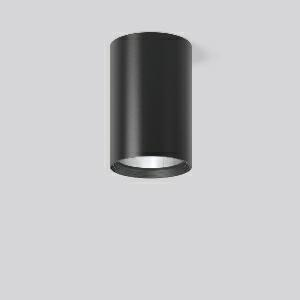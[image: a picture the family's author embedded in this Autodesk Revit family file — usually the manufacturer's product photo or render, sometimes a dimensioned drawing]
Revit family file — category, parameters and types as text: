
# Revit family: heledon_maxi_a_931219_003_3_76_b0ef
name_source: partatom
category: Lighting Fixtures
units: mm (PartAtom-declared; Revit-internal decimal feet)

## family parameters
Cut with Voids When Loaded = No
Host = Face
Light Source = No
Part Type = Normal
Room Calculation Point = No
Round Connector Dimension = Use Diameter
Shared = No

## types (1)
- HELEDON maxi A (1 x LED Modul 935, 3250 lm, 3500)
    Apparent Load = 25 VA
    Approval mark = CE
    CIE Flux Codes = 97 100 100 100 100
    Color Rendering = 92
    Color Temperature = 3500
    Default Elevation = 1800 mm
    Description = Series: HELEDON maxi
Cylindrical surface-mounted downlight. Housing: die-cast aluminium, powder-coated. Internal ceiling frame polycarbonate with bayonet mounting. Black plastic ring and recessed LED to prevent glare from the side. Optical assembly with reflector made of MIRO-Silver with 98% total light reflection for outstanding efficiency - can be changed without tools. Best colour rendering index Ra>90. Suitable for Ceiling mounting. Easy installation with a separate ceiling frame with bayonet mounting and plug connection. Driver integrated. Connected via plug-in connector. High quality converter without flickering and stroboscopic effect. The following accessories can be mounted without use of tools: interchangeable lenses, decorative glasses, honeycomb louvre, clear and frosted diffusers, white interchangeable plastic ring. 
Colour: deep black, matt (RAL 9005)
Diameter: 123 mm
Height: 183 mm
Lamp: LED
Socket: without socket
Colour temperature: 3500K
Colour rendering index (CRI): 92
System power: 25 W
Rated luminous flux: 3250 lm
Luminous efficiency: 130 lm/W
Control gear: Converter, dimmable, DALI
Protection class: I
Type of protection: IP 20
    Height = 183 mm
    Lamp = 1 x LED Modul 935
    Lamp Light Flux = 3250 lm
    Lamp count = 1
    Length = 123 mm
    Lifetime = 50000 h
    Luminous efficacy = 130 lm/W
    Manufacturer = RZB
    ModVariant = No
    Model = 931219.003.3.76
    Mounting Place = Ceiling
    Mounting Type = Surface mounted
    Number of Poles = 1
    OnlyDefault = Yes
    Power Factor = 1
    Product Name = HELEDON maxi A
    Product group = Surface mounted downlights
    ProductGroupID = 302
    Protection Class = Protection class I
    Protection Degree = IP 20
    RLX_Detail_Level = 1
    RLX_Emergency_Light_Flux = 0 lm
    RLX_Emergency_Type = 0
    RLX_Emergency_Type_DB = No
    RlxData = <blob elided: 97689 chars, md5=1b55310d>
    Socket = socket
    Standby Power = 0 W
    System Light Flux = 3250 lm
    System Power = 25 W
    Type Comments = Product without accessories
    Type Image = 931192.003.jpg
    URL = http://relux.com
    VarID = ---
    Voltage = 230 V
    Voltage Range = 220-240 V
    Weight = 0.00 kg
    Width = 0 mm  [stored 0 ft]

note: [stored X ft] marks values corroborated as IEEE doubles in the binary element streams (Revit-internal decimal feet)

## geometry (parser evidence)
native form markers: Blend x4, Sweep x10
no freeform markers — native parametric forms only
